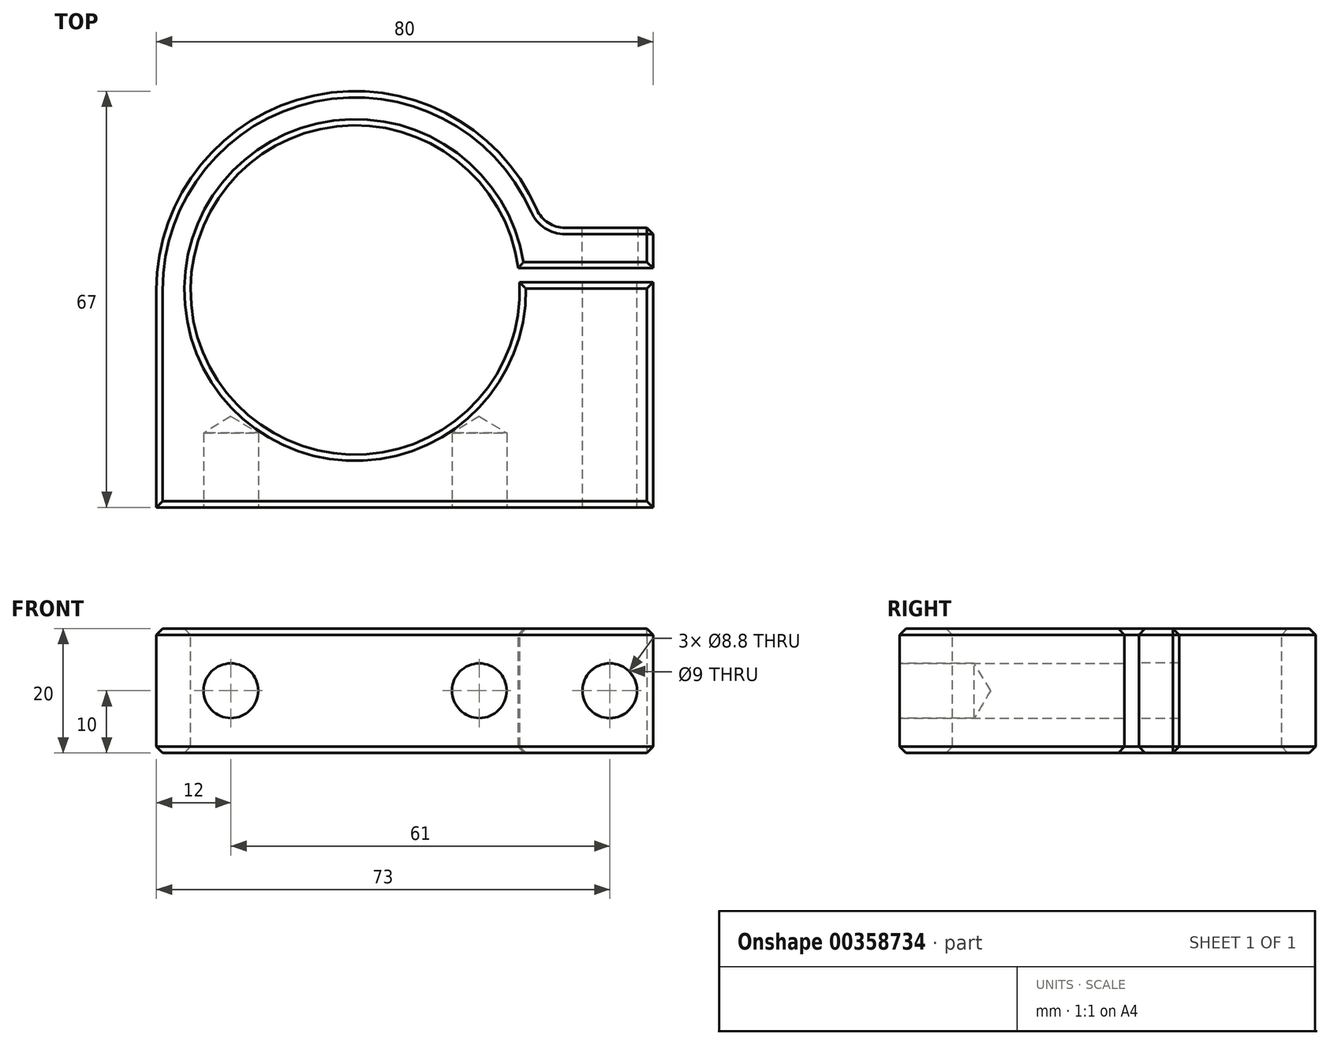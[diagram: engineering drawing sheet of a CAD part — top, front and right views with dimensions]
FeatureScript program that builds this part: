
annotation { "Feature Type Name" : "Feature", "Feature Type Description" : "" }
export const myFeature = defineFeature(function(context is Context, id is Id, definition is map)
    precondition{}
    {
        {
            var Q0;
            Q0=qCreatedBy(makeId("Top.planeOp"),FACE);
            var sketch = newSketch(context, id + "F0", { "sketchPlane" : qUnion([Q0])});
            skLineSegment(sketch, "E0.right", {"start": v(-32, 17.5) * mm, "end": v(-32, -17.5) * mm});
            skPoint(sketch, "E0.middle", {"position": v(0, 0) * mm});
            skArc(sketch, "E1", {"start": v(30.4, 27.5) * mm, "mid": v(-5.06, 49.1) * mm, "end": v(-32, 17.5) * mm});
            skLineSegment(sketch, "E2", {"start": v(-32, -17.5) * mm, "end": v(48, -17.5) * mm});
            skLineSegment(sketch, "E3", {"start": v(48, 27.5) * mm, "end": v(30.4, 27.5) * mm});
            skLineSegment(sketch, "E4", {"start": v(48, 27.5) * mm, "end": v(48, -17.5) * mm});
            skSolve(sketch);
        }
        {
            var Q0;
            Q0 = qSketchRegion(id + "F0", true);
            extrude(context, id + "F1", {"entities" : qUnion([Q0]), "depth" : 20 * mm});
        }
        {
            var Q0;
            Q0=makeQuery(id+"F1.opExtrude","CAP_FACE",FACE,{"disambiguationData":[OSD([sQuery(id+"F0.wireOp",EDGE,"E0.top"),sQuery(id+"F0.wireOp",EDGE,"E0.left"),sQuery(id+"F0.wireOp",EDGE,"E0.right"),sQuery(id+"F0.wireOp",EDGE,"E1")])],"isStart":false});
            var sketch = newSketch(context, id + "F2", { "sketchPlane" : qUnion([Q0])});
            skCircle(sketch, "E5", {"center": v(0, 17.5) * mm, "radius": 26.5 * mm});
            skSolve(sketch);
        }
        {
            var Q0;
            Q0 = qSketchRegion(id + "F2", true);
            extrude(context, id + "F3", {"entities" : qUnion([Q0]), "operationType" : NewBodyOperationType.REMOVE, "endBound" : BoundingType.UP_TO_NEXT, "oppositeDirection" : true, "depth" : 25 * mm});
        }
        {
            var Q0;
            Q0=makeQuery(id+"F1.opExtrude","CAP_FACE",FACE,{"disambiguationData":[OSD([sQuery(id+"F0.wireOp",EDGE,"E0.right"),sQuery(id+"F0.wireOp",EDGE,"E1"),sQuery(id+"F0.wireOp",EDGE,"E2"),sQuery(id+"F0.wireOp",EDGE,"E3"),sQuery(id+"F0.wireOp",EDGE,"E4")])],"isStart":false});
            var sketch = newSketch(context, id + "F4", { "sketchPlane" : qUnion([Q0])});
            skLineSegment(sketch, "E6.bottom", {"start": v(20, 21.02) * mm, "end": v(70, 21.02) * mm});
            skLineSegment(sketch, "E6.top", {"start": v(20, 18.72) * mm, "end": v(70, 18.72) * mm});
            skLineSegment(sketch, "E6.left", {"start": v(20, 21.02) * mm, "end": v(20, 18.72) * mm});
            skLineSegment(sketch, "E6.right", {"start": v(70, 21.02) * mm, "end": v(70, 18.72) * mm});
            skSolve(sketch);
        }
        {
            var Q0;
            Q0 = qSketchRegion(id + "F4", true);
            extrude(context, id + "F5", {"entities" : qUnion([Q0]), "operationType" : NewBodyOperationType.REMOVE, "endBound" : BoundingType.THROUGH_ALL, "oppositeDirection" : true, "depth" : 25 * mm});
        }
        {
            var Q0;
            Q0=makeQuery(id+"F1.opExtrude","SWEPT_FACE",FACE,{"disambiguationData":[OSD([sQuery(id+"F0.wireOp",EDGE,"E2")])]});
            var sketch = newSketch(context, id + "F6", { "sketchPlane" : qUnion([Q0])});
            skPoint(sketch, "E7", {"position": v(-20, 10) * mm});
            skLineSegment(sketch, "E8", {"start": v(-20, 20) * mm, "end": v(-20, 0) * mm, "construction": true});
            skPoint(sketch, "E9.MirrorP", {"position": v(20, 10) * mm});
            skSolve(sketch);
        }
        {
            var Q0;
            Q0=sQuery(id+"F6.wireOp",VERTEX,"E7");
            var Q1;
            Q1=sQuery(id+"F6.wireOp",VERTEX,"E9.MirrorP");
            var Q2;
            Q2=makeQuery(id+"F1.opExtrude","SWEPT_BODY",BODY,{"disambiguationData":[OSD([sQuery(id+"F0.wireOp",EDGE,"E0.right"),sQuery(id+"F0.wireOp",EDGE,"E1"),sQuery(id+"F0.wireOp",EDGE,"E2"),sQuery(id+"F0.wireOp",EDGE,"E3"),sQuery(id+"F0.wireOp",EDGE,"E4")])]});
            hole(context, id + "F7", {"style" : HoleStyle.SIMPLE, "endStyle" : HoleEndStyle.BLIND, "standardTappedOrClearance" : lookupTablePath({ "standard" : "ISO", "fit" : "Normal", "size" : "M8", "type" : "Clearance" }), "standardBlindInLast" : lookupTablePath({ "fit" : "Standard", "standard" : "ISO", "size" : "M8", "type" : "Clearance" }), "holeDiameter" : 8.8 * mm, "holeDepth" : 12 * mm, "isTappedThrough" : true, "tappedDepth" : 12 * mm, "tapClearance" : 3, "locations" : qUnion([Q0, Q1]), "scope" : qUnion([Q2])});
        }
        {
            var Q0;
            Q0=makeQuery(id+"F1.opExtrude","SWEPT_EDGE",EDGE,{"disambiguationData":[OSD([sQuery(id+"F0.wireOp",EDGE,"E1"),sQuery(id+"F0.wireOp",EDGE,"E3")])]});
            fillet(context, id + "F8", {"entities" : qUnion([Q0]), "radius" : 5 * mm, "tangentPropagation" : true, "allowEdgeOverflow" : false});
        }
        {
            var Q0;
            Q0=makeQuery(id+"F5.boolean.opBoolean","COPY",FACE,{"derivedFrom":makeQuery(id+"F5.opExtrude","SWEPT_FACE",FACE,{"disambiguationData":[OSD([sQuery(id+"F4.wireOp",EDGE,"E6.top")])]})});
            var sketch = newSketch(context, id + "F9", { "sketchPlane" : qUnion([Q0])});
            skPoint(sketch, "E10", {"position": v(-41, 10) * mm});
            skLineSegment(sketch, "E11", {"start": v(-41, 0) * mm, "end": v(-41, 20) * mm});
            skSolve(sketch);
        }
        {
            var Q0;
            Q0=sQuery(id+"F9.wireOp",VERTEX,"E10");
            var Q1;
            Q1=makeQuery(id+"F1.opExtrude","SWEPT_BODY",BODY,{"disambiguationData":[OSD([sQuery(id+"F0.wireOp",EDGE,"E0.right"),sQuery(id+"F0.wireOp",EDGE,"E1"),sQuery(id+"F0.wireOp",EDGE,"E2"),sQuery(id+"F0.wireOp",EDGE,"E3"),sQuery(id+"F0.wireOp",EDGE,"E4")])]});
            hole(context, id + "F10", {"style" : HoleStyle.SIMPLE, "endStyle" : HoleEndStyle.THROUGH, "standardTappedOrClearance" : lookupTablePath({ "standard" : "ISO", "fit" : "Normal", "size" : "M8", "type" : "Clearance" }), "standardBlindInLast" : lookupTablePath({ "fit" : "Standard", "standard" : "ISO", "size" : "M8", "type" : "Clearance" }), "holeDiameter" : 8.8 * mm, "isTappedThrough" : true, "tappedDepth" : 12 * mm, "tapClearance" : 3, "locations" : qUnion([Q0]), "scope" : qUnion([Q1])});
        }
        {
            var Q0;
            Q0=sQuery(id+"F9.wireOp",VERTEX,"E10");
            var Q1;
            Q1=makeQuery(id+"F1.opExtrude","SWEPT_BODY",BODY,{"disambiguationData":[OSD([sQuery(id+"F0.wireOp",EDGE,"E0.right"),sQuery(id+"F0.wireOp",EDGE,"E1"),sQuery(id+"F0.wireOp",EDGE,"E2"),sQuery(id+"F0.wireOp",EDGE,"E3"),sQuery(id+"F0.wireOp",EDGE,"E4")])]});
            hole(context, id + "F11", {"style" : HoleStyle.SIMPLE, "endStyle" : HoleEndStyle.THROUGH, "oppositeDirection" : true, "holeDiameter" : 9 * mm, "isTappedThrough" : true, "tappedDepth" : 12 * mm, "tapClearance" : 3, "locations" : qUnion([Q0]), "scope" : qUnion([Q1])});
        }
        {
            var Q0;
            Q0=makeQuery(id+"F1.opExtrude","CAP_FACE",FACE,{"disambiguationData":[OSD([sQuery(id+"F0.wireOp",EDGE,"E0.right"),sQuery(id+"F0.wireOp",EDGE,"E1"),sQuery(id+"F0.wireOp",EDGE,"E2"),sQuery(id+"F0.wireOp",EDGE,"E3"),sQuery(id+"F0.wireOp",EDGE,"E4")])],"isStart":false});
            var Q1;
            Q1=makeQuery(id+"F1.opExtrude","CAP_FACE",FACE,{"disambiguationData":[OSD([sQuery(id+"F0.wireOp",EDGE,"E0.right"),sQuery(id+"F0.wireOp",EDGE,"E1"),sQuery(id+"F0.wireOp",EDGE,"E2"),sQuery(id+"F0.wireOp",EDGE,"E3"),sQuery(id+"F0.wireOp",EDGE,"E4")])],"isStart":true});
            var Q2;
            Q2=makeQuery(id+"F1.opExtrude","SWEPT_EDGE",EDGE,{"disambiguationData":[OSD([sQuery(id+"F0.wireOp",EDGE,"E3"),sQuery(id+"F0.wireOp",EDGE,"E4")])]});
            chamfer(context, id + "F12", {"entities" : qUnion([Q0, Q1, Q2]), "width" : 1 * mm, "tangentPropagation" : true});
        }
    });
